# Revit family: rba-bim-rba8841 Series
name_source: partatom
category: Plumbing Fixtures
revit_build: Autodesk Revit 2018 (Build: 20170223_1515(x64)
units: mm (PartAtom-declared; Revit-internal decimal feet)

## family parameters
Always vertical = Yes
Cut with Voids When Loaded = No
OmniClass Number = 23.45.00.00
OmniClass Title = Sanitary, Laundry, and Cleaning Equipment
Part Type = Normal
Room Calculation Point = No
Round Connector Dimension = Use Diameter
Shared = No
Work Plane-Based = No

## types (2) — shared parameters
Inlet (Internal Diameter) = 55 mm  [stored 0.180446 ft]
Installation Instructions = www.rba.com.au/toilets-urinals/toilets
Manufacturer = RBA Group
Materials and Finishes = Stainless Steel - Satin
Oulet (Outside Diameter) = 100 mm  [stored 0.328084 ft]
Specifier = RBA Group
Technical Data Sheet = www.rba.com.au/toilets-urinals/toilets
URL = www.rba.com.au/toilets-urinals/toilets

## per-type parameters (varying)
| type | Description | Model | Modified Issue |
| RBA8841-100 Front Fixed | Wall Faced WC Pan with P-Trap Outlet - Front Fixed | RBA8841-100 | 20200501.01 |
| RBA8841-144 Rear Fixed | Wall Faced WC Pan with P-Trap Outlet - Rear Fixed | RBA8841-144 |  |

note: [stored X ft] marks values corroborated as IEEE doubles in the binary element streams (Revit-internal decimal feet)

## geometry (parser evidence)
native form markers: Blend x8, Sweep x1
no freeform markers — native parametric forms only
